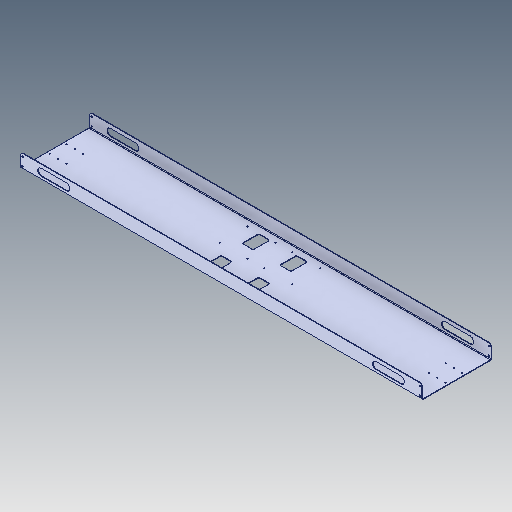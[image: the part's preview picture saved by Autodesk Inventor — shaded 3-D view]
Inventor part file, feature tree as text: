
AUTODESK INVENTOR PART (.ipt)
format: ipt  version: 2023.5 (Build 275446000, 446)  size: 178,688 bytes
history: native  units: in
note: dims shown in document units (in); Inventor stores cm internally (conversion verified against a paired STEP export)
features: mirror x1
ambient origin geometry x8: Origin, YZ Plane, XZ Plane, XY Plane, X Axis, Y Axis, Z Axis, Center Point
bodies: Solid1 (feature_tree)
feature tree (1):
  mirror  "Mirror2"
